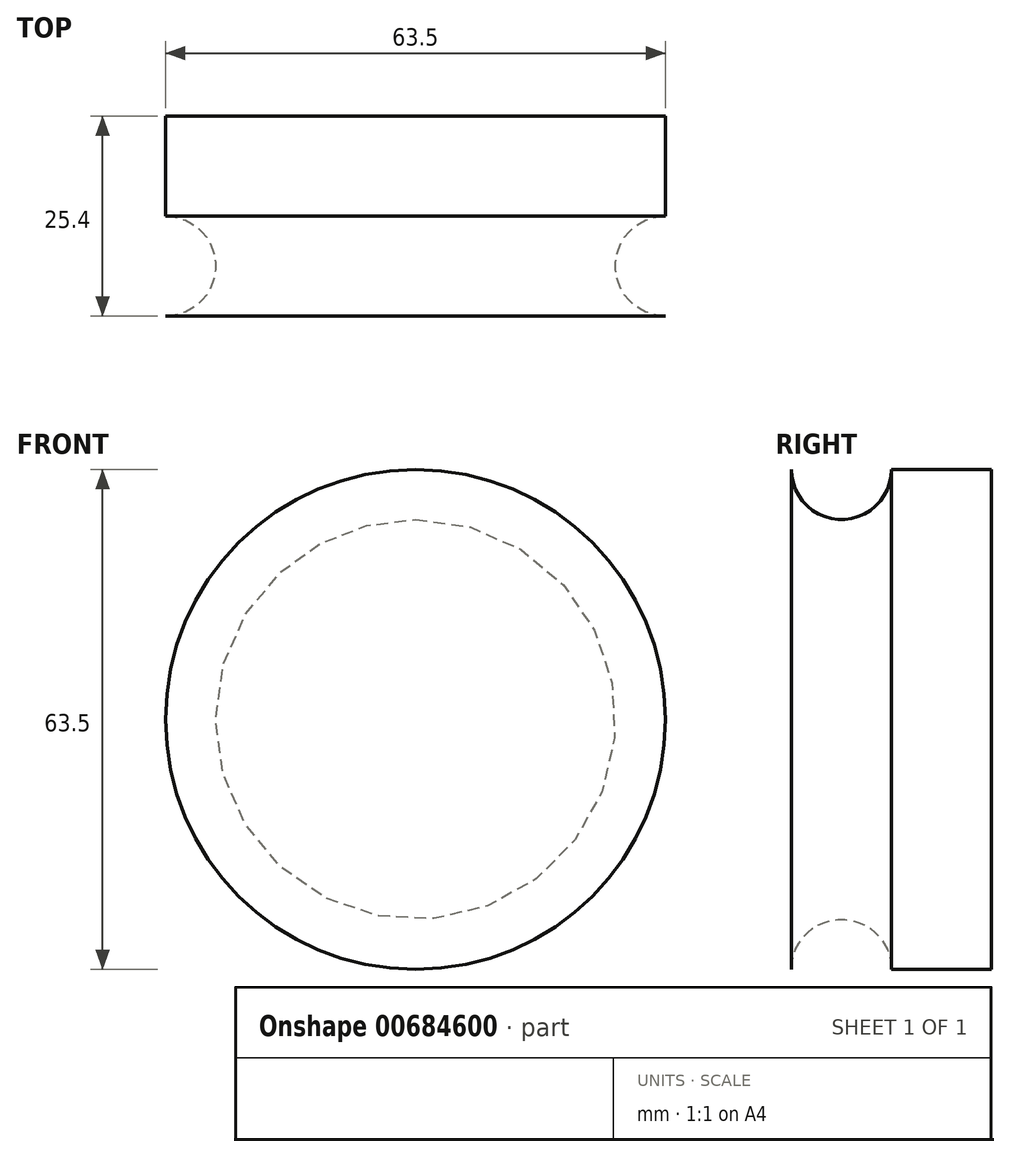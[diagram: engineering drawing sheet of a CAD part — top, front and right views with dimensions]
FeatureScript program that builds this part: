
annotation { "Feature Type Name" : "Feature", "Feature Type Description" : "" }
export const myFeature = defineFeature(function(context is Context, id is Id, definition is map)
    precondition{}
    {
        {
            var Q0;
            Q0=qCreatedBy(makeId("Front.planeOp"),FACE);
            var sketch = newSketch(context, id + "F0", { "sketchPlane" : qUnion([Q0])});
            skCircle(sketch, "E0", {"center": v(0, 0) * mm, "radius": 31.75 * mm});
            skSolve(sketch);
        }
        {
            var Q0;
            Q0 = qSketchRegion(id + "F0", false);
            extrude(context, id + "F1", {"entities" : qUnion([Q0]), "depth" : 25.4 * mm});
        }
        {
            var Q0;
            Q0=makeQuery(id+"F1.opExtrude","CAP_FACE",FACE,{"disambiguationData":[OSD([sQuery(id+"F0.wireOp",EDGE,"E0")])],"isStart":true});
            cPlane(context, id + "F2", {"entities" : qUnion([Q0]), "cplaneType" : CPlaneType.OFFSET, "offset" : 19.05 * mm, "oppositeDirection" : true, "width" : 152.4 * mm, "height" : 152.4 * mm});
        }
        {
            var Q0;
            Q0=qCreatedBy(id+"F2.planeOp",FACE);
            var sketch = newSketch(context, id + "F3", { "sketchPlane" : qUnion([Q0])});
            skCircle(sketch, "E0", {"center": v(0, 0) * mm, "radius": 31.75 * mm});
            skSolve(sketch);
        }
        {
            var Q0;
            Q0=qCreatedBy(makeId("Right.planeOp"),FACE);
            var sketch = newSketch(context, id + "F4", { "sketchPlane" : qUnion([Q0])});
            skCircle(sketch, "E1", {"center": v(-19.05, 31.75) * mm, "radius": 6.35 * mm});
            skSolve(sketch);
        }
        {
            var Q0;
            Q0=makeQuery(id+"F4.imprint","IMPRINT",FACE,{"disambiguationData":[TD([[makeQuery(id+"F4.imprint","IMPRINT",EDGE,{"derivedFrom":sQuery(id+"F4.wireOp",EDGE,"E1")}),1.0]])]});
            var Q1;
            Q1=sQuery(id+"F3.wireOp",EDGE,"E0");
            sweep(context, id + "F5", {"operationType" : NewBodyOperationType.REMOVE, "profiles" : qUnion([Q0]), "path" : qUnion([Q1])});
        }
    });
